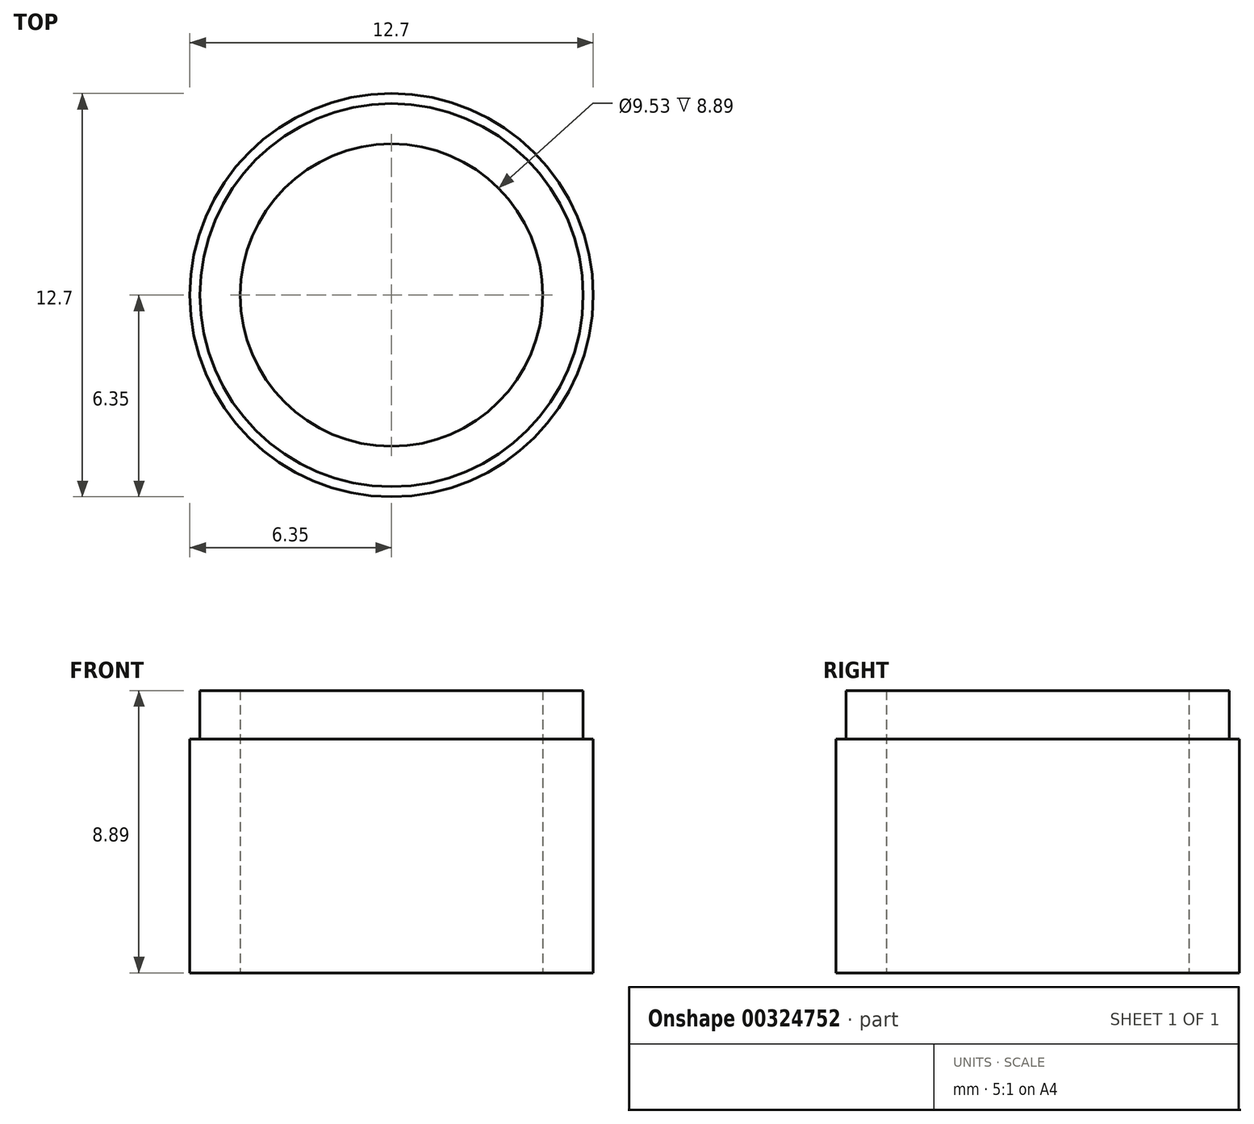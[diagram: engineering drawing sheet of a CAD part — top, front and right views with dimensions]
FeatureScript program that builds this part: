
annotation { "Feature Type Name" : "Feature", "Feature Type Description" : "" }
export const myFeature = defineFeature(function(context is Context, id is Id, definition is map)
    precondition{}
    {
        {
            var Q0;
            Q0=qCreatedBy(makeId("Top.planeOp"),FACE);
            var sketch = newSketch(context, id + "F0", { "sketchPlane" : qUnion([Q0])});
            skCircle(sketch, "E0", {"center": v(0, 0) * mm, "radius": 6.35 * mm});
            skCircle(sketch, "E1", {"center": v(0, 0) * mm, "radius": 4.76 * mm});
            skSolve(sketch);
        }
        {
            var Q0;
            Q0=makeQuery(id+"F0.imprint","IMPRINT",FACE,{"disambiguationData":[TD([[makeQuery(id+"F0.imprint","IMPRINT",EDGE,{"derivedFrom":sQuery(id+"F0.wireOp",EDGE,"E0")}),1.0]])]});
            extrude(context, id + "F1", {"entities" : qUnion([Q0]), "depth" : 8.9 * mm, "offsetDistance" : 25.4 * mm});
        }
        {
            var Q0;
            Q0=makeQuery(id+"F1.opExtrude","CAP_FACE",FACE,{"disambiguationData":[OSD([sQuery(id+"F0.wireOp",EDGE,"E0"),sQuery(id+"F0.wireOp",EDGE,"E1")])],"isStart":false});
            var sketch = newSketch(context, id + "F2", { "sketchPlane" : qUnion([Q0])});
            skCircle(sketch, "E2", {"center": v(0, 0) * mm, "radius": 6.03 * mm});
            skCircle(sketch, "E3", {"center": v(0, 0) * mm, "radius": 6.35 * mm});
            skSolve(sketch);
        }
        {
            var Q0;
            Q0=makeQuery(id+"F2.imprint","IMPRINT",FACE,{"disambiguationData":[TD([[makeQuery(id+"F2.imprint","IMPRINT",EDGE,{"derivedFrom":sQuery(id+"F2.wireOp",EDGE,"E2")}),-1.0]])]});
            extrude(context, id + "F3", {"entities" : qUnion([Q0]), "operationType" : NewBodyOperationType.REMOVE, "oppositeDirection" : true, "depth" : 1.52 * mm, "offsetDistance" : 25.4 * mm});
        }
    });
